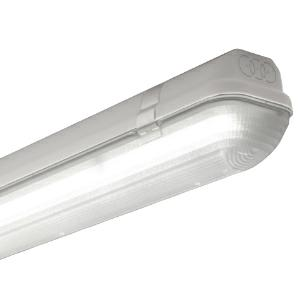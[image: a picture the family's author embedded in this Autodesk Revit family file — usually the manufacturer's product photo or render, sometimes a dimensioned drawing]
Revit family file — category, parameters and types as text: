
# Revit family: 3f_filippi_-_3f_linda_3f_filippi_-_58606_-_3f_linda_led_1x30w-865_l1570
name_source: partatom
category: Lighting Fixtures
units: mm (PartAtom-declared; Revit-internal decimal feet)

## family parameters
Cut with Voids When Loaded = No
Host = Face
Light Source = No
Part Type = Normal
Room Calculation Point = No
Round Connector Dimension = Use Diameter
Shared = No

## types (1)
- 3F Filippi - 3F Linda (1 x LED, 5180 lm, 33.5 W, 6500 K)
    Apparent Load = 34 VA
    Approval mark = CE
    CIE Flux Codes = 44 77 94 97 100
    Color Rendering = 80
    Color Temperature = 6500 K
    Control Gear = Electronic ballast
    Default Elevation = 1800 mm
    Description = ILLUMINOTECHNICAL
Luminous efficiency 100% (DLOR 97%, ULOR 3%).
Initial luminous flux of the luminaire 5180 lm.
Controlled symmetric distribution.
Installation Interdistance Transv.D = 1.77 x hu - Long.D = 1.17 x hu.
Tabular UGR (CIE 117 - 4H-8H; S=0.25H; 70/50/20): RUG 22.1 - 23.1.
Beam angle: 109° - 64°.
Luminous efficacy 155 lm/W.
Lifetime (L93/B10): 30000 h. (tq+25°C)
Lifetime (L90/B10): 50000 h. (tq+25°C)
Lifetime (L85/B10): 80000 h. (tq+25°C)
Lifetime (L80/B10): 100000 h. (tq+25°C)
Lifetime (L85/B10): 50000 h. (tq+35°C)
Sudden decreased luminous flux after 50000 hours: 0% (C0).
Photobiological safety in compliance with IEC/TR 62778: RG0 risk exempt, (IEC 62471).
In compliance with IEC/EN 62722-2-1 - IEC/EN 62717 standards.

SOURCE
Linear LED module 30W/865.
Energy efficiency class (UE 2019/2020 - UE 2019/2015): C.
CIE 13.3 Colour rendering index: CRI >80 (R9 <50%).
IES TM-30 Fidelity Index: Rf = 84 Rg = 95.
CCT nominal colour temperature 6500 K.
Colour initial tolerance (MacAdam): SDCM 3.

MECHANICAL
Self-extinguishing V2 polycarbonate housing, injection moulded, RAL 7035 grey.
Ecologic anti-aging injected sealing gasket.
Diffuser in self-extinguishing V2 polycarbonate, photo-engraved interior, UV stabilised, injection moulded with smooth outer surface, tamper-proof opening.
Gear-holder reflector in hot-dip galvanised steel, painted with white polyester base.
Snug fit safety snap-lock clips for diffuser mounting in stainless steel, screwdriver opening.
Fixing brackets in stainless steel.
Possibility for technicians to access the interior of the luminaire.
Luminaire with limited surface temperature. - D - (EN 60598-2-24)
Dimensions: 1570x100 mm, height 100 mm. Weight 2.5 kg.
IP66 protection degree.
Mechanical strength to impacts IK10 (20 joule).
Glow-wire test resistance 850°C.

ELECTRICAL
Halogen Free electronic wiring 230V-50/60Hz, power factor 0.90, THD <25%, constant output current, SELV, class I, 1 driver.
Power of the luminaire 33.5 W.
ENEC - CE.
SAFE FLICKER: PstLM=<1 and SVM=<0.4 (IEC TR 61547-1 and IEC TR 63158), to ensure a more comfortable and safe light.
Luminaire compliant with EN 60598-2-22 for power supply from a centralised emergency system CPSS (Central Power Supply System), not incorporated in the luminaire - high risk areas excluded. The default power and flux are 100% in AC and 100% in DC.
Ambient temperature from -20°C to +35°C.
Temperature class T6 max 85°C.
Relative humidity UR: <85%.

INSTALLATION
Ceiling / Suspended / Wall.
All accessories dedicated to this product are available on the Catalog and on our website www.3F-Filippi.com.

APPLICATIONS
Suitable product for food production plants (HACCP), IFS (Food Version 6), BRC (GSFS Food Version 7).
Dry, dusty indoor environments, subject to occasional water splashes.
Virtually shatterproof polycarbonate compatibly with the fumes / atmospheres that compromise the elasticity of plastic materials.
Not suitable for installation on surfaces subject to important vibrations, exposed to weather conditions, on ropes or poles.
Suitable for illumination of public car parks and parking grounds referred to DIN 67528:2018-04.

WARNING
Fixture not suitable for cold stores with an ambient temperature <0°C and/or relative humidity >85%.
Luminaire designed for disposal/recycling at end-of-life.
Replaceable (LED only) light source by a professional. Replaceable control gear by a professional.
    Height = 100 mm  [stored 0.328084 ft]
    Lamp = 1 x LED
    Lamp Light Flux = 5180 lm
    Lamp Power = 33.5 W
    Lamp count = 1
    Length = 1570 mm
    Lifetime = 50000 h
    Luminous efficacy = 155 lm/W
    Manufacturer = 3F Filippi
    ModVariant = No
    Model = 3F Filippi - 58606 - 3F Linda LED 1x30W-865 L1570
    Mounting Place = Ceiling
    Mounting Type = Pendant
    Number of Poles = 1
    OnlyDefault = Yes
    Power Factor = 1
    Product Name = 3F Filippi - 3F Linda
    Product group = pendant luminaire
    ProductGroupID = 9
    Protection Class = Protection class I
    Protection Degree = IP 66
    RLX_Detail_Level = 1
    RLX_Emergency_Light_Flux = 0 lm
    RLX_Emergency_Type = 0
    RLX_Emergency_Type_DB = No
    RlxData = <blob elided: 70909 chars, md5=741ff050>
    Socket = socket
    Standby Power = 0 W
    System Light Flux = 5180 lm
    System Power = 34 W
    Type Comments = Product without accessories
    Type Image = 3ffilippi_3f_linda_led.jpg
    URL = http://relux.com
    VarID = ---
    Voltage = 0 V
    Weight = 0.00 kg
    Width = 100 mm  [stored 0.328084 ft]

note: [stored X ft] marks values corroborated as IEEE doubles in the binary element streams (Revit-internal decimal feet)

## geometry (parser evidence)
native form markers: Blend x4, Sweep x9
no freeform markers — native parametric forms only
